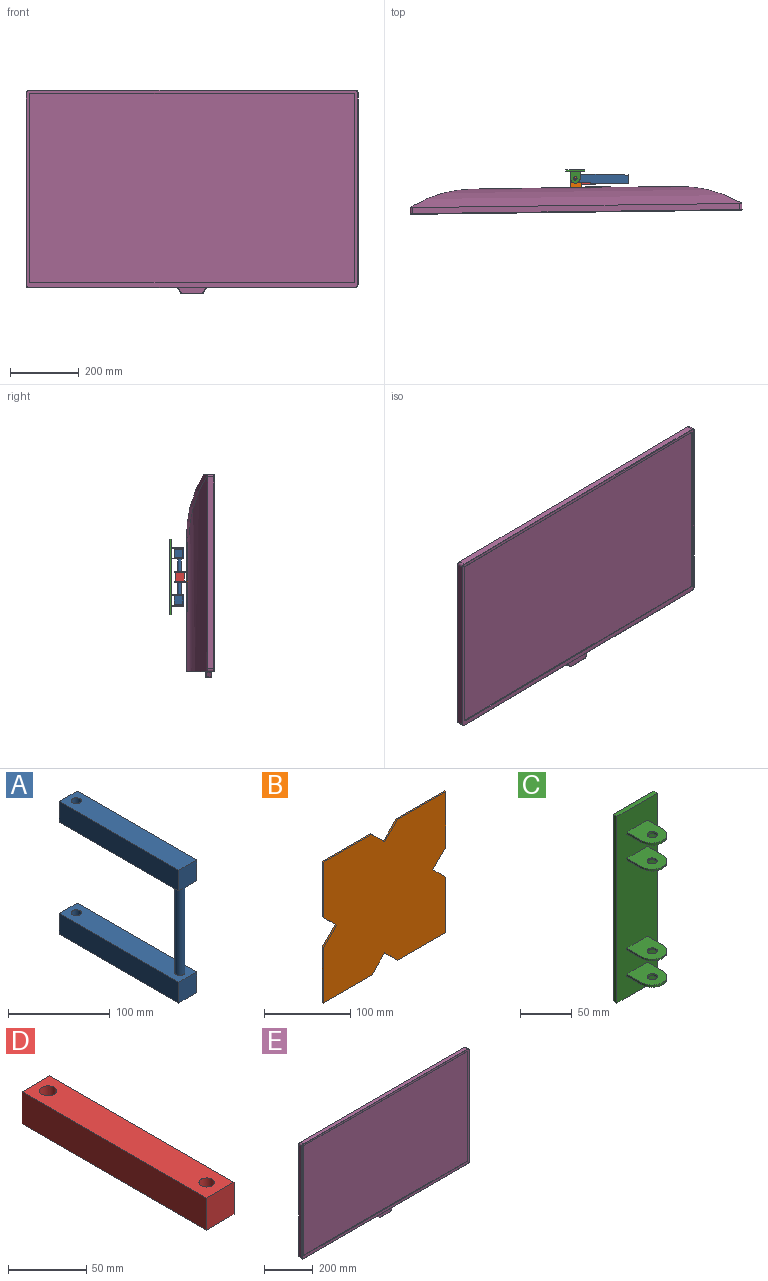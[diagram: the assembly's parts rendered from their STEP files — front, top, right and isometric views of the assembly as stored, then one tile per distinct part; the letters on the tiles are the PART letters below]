
ASSEMBLY  parts=5 mates=4
PART A: 15 faces, bbox 25x166x160 mm
  f0: plane 166x25mm, normal (-1,0,0), area 4150mm2, adj f1,f3,f5,f7
  f1: plane 25x25mm, normal (0,-1,0), area 625mm2, adj f0,f2,f5,f7
  f2: plane 166x25mm, normal (1,0,0), area 4150mm2, adj f1,f3,f5,f7
  f3: plane 25x25mm, normal (0,1,0), area 625mm2, adj f0,f2,f5,f7
  f4: cylinder r=5mm len=25mm, axis (0,0,-1), area 785.4mm2, adj f5,f7
  f5: plane 166x25mm, normal (0,0,1), area 4071.5mm2, adj f0,f1,f2,f3,f4
  f6: cylinder r=5mm len=110mm, axis (0,0,-1), area 3455.8mm2, adj f7,f8
  f7: plane 166x25mm, normal (0,0,-1), area 3992.9mm2, adj f0,f1,f2,f3,f4,f6
  f8: plane 166x25mm, normal (0,0,1), area 3992.9mm2, adj f6,f9,f10,f11,f12,f14
  f9: plane 25x25mm, normal (0,1,0), area 625mm2, adj f8,f10,f12,f13
  f10: plane 166x25mm, normal (1,0,0), area 4150mm2, adj f8,f9,f11,f13
  f11: plane 25x25mm, normal (0,-1,0), area 625mm2, adj f8,f10,f12,f13
  f12: plane 166x25mm, normal (-1,0,0), area 4150mm2, adj f8,f9,f11,f13
  f13: plane 166x25mm, normal (0,0,-1), area 4071.5mm2, adj f9,f10,f11,f12,f14
  f14: cylinder r=5mm len=25mm, axis (0,0,-1), area 785.4mm2, adj f8,f13
PART B: 30 faces, bbox 200x39x200 mm
  f0: plane 21x2.5mm, normal (-1,0,0), area 52.5mm2, adj f2,f4,f5,f6
  f1: plane 21x2.5mm, normal (1,0,0), area 52.5mm2, adj f2,f4,f5,f6
  f2: cylinder r=16mm len=32mm, axis (0,0,-1), area 125.7mm2, adj f0,f1,f4,f5
  f3: cylinder r=5mm len=10mm, axis (0,0,-1), area 78.5mm2, adj f4,f5
  f4: plane 37x32mm, normal (0,0,-1), area 995.6mm2, adj f0,f1,f2,f3,f6
  f5: plane 37x32mm, normal (0,0,1), area 995.6mm2, adj f0,f1,f2,f3,f6
  f6: plane 200x200mm, normal (0,1,0), area 38040mm2, adj f0,f1,f4,f5,f7,f8,f10,f12
  f7: plane 21x2.5mm, normal (1,0,0), area 52.5mm2, adj f6,f9,f10,f12
  f8: plane 21x2.5mm, normal (-1,0,0), area 52.5mm2, adj f6,f9,f10,f12
  f9: cylinder r=16mm len=32mm, axis (0,0,-1), area 125.7mm2, adj f7,f8,f10,f12
  f10: plane 37x32mm, normal (0,0,1), area 995.6mm2, adj f6,f7,f8,f9,f11
  f11: cylinder r=5mm len=10mm, axis (0,0,-1), area 78.5mm2, adj f10,f12
  f12: plane 37x32mm, normal (0,0,-1), area 995.6mm2, adj f6,f7,f8,f9,f11
  f13: plane 21.21x21.21mm, normal (0.71,0,0.71), area 60mm2, adj f6,f14,f28,f29
  f14: plane 78.79x2mm, normal (0,0,1), area 157.6mm2, adj f6,f13,f15,f29
  f15: plane 78.79x2mm, normal (-1,0,0), area 157.6mm2, adj f6,f14,f16,f29
  f16: plane 21.21x21.21mm, normal (-0.71,0,-0.71), area 60mm2, adj f6,f15,f17,f29
  f17: plane 21.21x21.21mm, normal (-0.71,0,0.71), area 60mm2, adj f6,f16,f18,f29
  f18: plane 78.79x2mm, normal (-1,0,0), area 157.6mm2, adj f6,f17,f19,f29
  f19: plane 78.79x2mm, normal (0,0,-1), area 157.6mm2, adj f6,f18,f20,f29
  f20: plane 21.21x21.21mm, normal (0.71,0,-0.71), area 60mm2, adj f6,f19,f21,f29
  f21: plane 21.21x21.21mm, normal (-0.71,0,-0.71), area 60mm2, adj f6,f20,f22,f29
  f22: plane 78.79x2mm, normal (0,0,-1), area 157.6mm2, adj f6,f21,f23,f29
  f23: plane 78.79x2mm, normal (1,0,0), area 157.6mm2, adj f6,f22,f24,f29
  f24: plane 21.21x21.21mm, normal (0.71,0,0.71), area 60mm2, adj f6,f23,f25,f29
  f25: plane 21.21x21.21mm, normal (0.71,0,-0.71), area 60mm2, adj f6,f24,f26,f29
  f26: plane 78.79x2mm, normal (1,0,0), area 157.6mm2, adj f6,f25,f27,f29
  f27: plane 78.79x2mm, normal (0,0,1), area 157.6mm2, adj f6,f26,f28,f29
  f28: plane 21.21x21.21mm, normal (-0.71,0,0.71), area 60mm2, adj f6,f13,f27,f29
  f29: plane 200x200mm, normal (0,-1,0), area 38200mm2, adj f13,f14,f15,f16,f17,f18,f19,f20
PART C: 30 faces, bbox 55x39.5x220 mm
  f0: plane 20.5x2mm, normal (1,0,0), area 41mm2, adj f3,f8,f27,f28
  f1: plane 20.5x2mm, normal (-1,0,0), area 41mm2, adj f3,f8,f27,f28
  f2: cylinder r=5mm len=10mm, axis (0,0,-1), area 62.8mm2, adj f27,f28
  f3: cylinder r=14mm len=28mm, axis (0,0,-1), area 88mm2, adj f0,f1,f27,f28
  f4: plane 20.5x2.5mm, normal (1,0,0), area 51.3mm2, adj f7,f8,f19,f20
  f5: plane 20.5x2.5mm, normal (-1,0,0), area 51.3mm2, adj f7,f8,f19,f20
  f6: cylinder r=5mm len=10mm, axis (0,0,-1), area 78.5mm2, adj f19,f20
  f7: cylinder r=14mm len=28mm, axis (0,0,-1), area 110mm2, adj f4,f5,f19,f20
  f8: plane 220x55mm, normal (0,-1,0), area 11848mm2, adj f0,f1,f4,f5,f9,f11,f12,f13
  f9: plane 220x5mm, normal (1,0,0), area 1100mm2, adj f8,f10,f12,f13
  f10: plane 220x55mm, normal (0,1,0), area 12100mm2, adj f9,f11,f12,f13
  f11: plane 220x5mm, normal (-1,0,0), area 1100mm2, adj f8,f10,f12,f13
  f12: plane 55x5mm, normal (0,0,1), area 275mm2, adj f8,f9,f10,f11
  f13: plane 55x5mm, normal (0,0,-1), area 275mm2, adj f8,f9,f10,f11
  f14: plane 20.5x2.5mm, normal (1,0,0), area 51.3mm2, adj f8,f17,f18,f21
  f15: plane 20.5x2.5mm, normal (-1,0,0), area 51.3mm2, adj f8,f17,f18,f21
  f16: cylinder r=5mm len=10mm, axis (0,0,-1), area 78.5mm2, adj f18,f21
  f17: cylinder r=14mm len=28mm, axis (0,0,-1), area 110mm2, adj f14,f15,f18,f21
  f18: plane 34.5x28mm, normal (0,0,1), area 803.3mm2, adj f8,f14,f15,f16,f17
  f19: plane 34.5x28mm, normal (0,0,-1), area 803.3mm2, adj f4,f5,f6,f7,f8
  f20: plane 34.5x28mm, normal (0,0,1), area 803.3mm2, adj f4,f5,f6,f7,f8
  f21: plane 34.5x28mm, normal (0,0,-1), area 803.3mm2, adj f8,f14,f15,f16,f17
  f22: plane 20.5x2mm, normal (1,0,0), area 41mm2, adj f8,f25,f26,f29
  f23: plane 20.5x2mm, normal (-1,0,0), area 41mm2, adj f8,f25,f26,f29
  f24: cylinder r=5mm len=10mm, axis (0,0,-1), area 62.8mm2, adj f26,f29
  f25: cylinder r=14mm len=28mm, axis (0,0,-1), area 88mm2, adj f22,f23,f26,f29
  f26: plane 34.5x28mm, normal (0,0,1), area 803.3mm2, adj f8,f22,f23,f24,f25
  f27: plane 34.5x28mm, normal (0,0,-1), area 803.3mm2, adj f0,f1,f2,f3,f8
  f28: plane 34.5x28mm, normal (0,0,1), area 803.3mm2, adj f0,f1,f2,f3,f8
  f29: plane 34.5x28mm, normal (0,0,-1), area 803.3mm2, adj f8,f22,f23,f24,f25
PART D: 8 faces, bbox 25x166x25 mm
  f0: plane 25x25mm, normal (0,1,0), area 625mm2, adj f1,f4,f5,f6
  f1: plane 166x25mm, normal (-1,0,0), area 4150mm2, adj f0,f2,f5,f6
  f2: plane 25x25mm, normal (0,-1,0), area 625mm2, adj f1,f4,f5,f6
  f3: cylinder r=5.5mm len=25mm, axis (0,0,-1), area 863.9mm2, adj f5,f6
  f4: plane 166x25mm, normal (1,0,0), area 4150mm2, adj f0,f2,f5,f6
  f5: plane 166x25mm, normal (0,0,1), area 3976.4mm2, adj f0,f1,f2,f3,f4,f7
  f6: plane 166x25mm, normal (0,0,-1), area 3976.4mm2, adj f0,f1,f2,f3,f4,f7
  f7: cylinder r=5mm len=25mm, axis (0,0,1), area 785.4mm2, adj f5,f6
PART E: 62 faces, bbox 968.3x70.6x594.1 mm
  f0: plane 951x17.6mm, normal (0,0,-1), area 15292.5mm2, adj f14,f15,f16,f19,f20,f26,f27,f33
  f1: plane 559.2x17.6mm, normal (1,0,0), area 9841.9mm2, adj f35,f38,f41,f47
  f2: plane 951x17.6mm, normal (0,0,1), area 16737.6mm2, adj f36,f38,f39,f48
  f3: plane 559.2x17.6mm, normal (-1,0,0), area 9841.9mm2, adj f37,f39,f40,f44
  f4: plane 599.87x390.64mm, normal (0,1,0), area 234330.6mm2, adj f34,f35,f36,f37
  f5: plane 547.2x0.6mm, normal (1,0,0), area 328.3mm2, adj f10,f52,f58,f61
  f6: plane 945x0.6mm, normal (0,0,-1), area 567mm2, adj f10,f55,f59,f61
  f7: plane 547.2x0.6mm, normal (-1,0,0), area 328.3mm2, adj f10,f50,f54,f55
  f8: plane 945x0.6mm, normal (0,0,1), area 567mm2, adj f10,f50,f52,f53
  f9: plane 965x573.2mm, normal (0,-1,0), area 30010.6mm2, adj f42,f43,f44,f45,f46,f47,f48,f49
  f10: plane 947x549.2mm, normal (0,-1,0), area 520091.5mm2, adj f5,f6,f7,f8,f50,f52,f55,f61
  f11: plane 12x11.69mm, normal (-0.87,0,-0.49), area 161.3mm2, adj f16,f17,f25,f32
  f12: plane 57.15x12mm, normal (0,0,-1), area 685.9mm2, adj f17,f18,f23,f30
  f13: plane 12x11.69mm, normal (0.87,0,-0.49), area 161.3mm2, adj f18,f19,f21,f28
  f14: plane 80.72x15.76mm, normal (0,1,0), area 1113.9mm2, adj f0,f20,f21,f22,f23,f24,f25,f26
  f15: plane 80.72x15.76mm, normal (0,-1,0), area 1113.9mm2, adj f0,f27,f28,f29,f30,f31,f32,f33
  f16: cylinder r=6mm len=12mm, axis (0,1,0), area 75.9mm2, adj f0,f11,f26,f33
  f17: cylinder r=6mm len=12mm, axis (0,-1,0), area 75.9mm2, adj f11,f12,f24,f31
  f18: cylinder r=6mm len=12mm, axis (0,-1,0), area 75.9mm2, adj f12,f13,f22,f29
  f19: cylinder r=6mm len=12mm, axis (0,1,0), area 75.9mm2, adj f0,f13,f20,f27
  f20: torus R=8mm, axis (0,-1,0), area 13.4mm2, adj f0,f14,f19,f21
  f21: cylinder r=2mm len=12.67mm, axis (-0.49,0,-0.87), area 42.2mm2, adj f13,f14,f20,f22
  f22: torus R=4mm, axis (0,-1,0), area 17.5mm2, adj f14,f18,f21,f23
  f23: cylinder r=2mm len=57.15mm, axis (-1,0,0), area 179.6mm2, adj f12,f14,f22,f24
  f24: torus R=4mm, axis (0,-1,0), area 17.5mm2, adj f14,f17,f23,f25
  f25: cylinder r=2mm len=12.67mm, axis (-0.49,0,0.87), area 42.2mm2, adj f11,f14,f24,f26
  f26: torus R=8mm, axis (0,-1,0), area 13.4mm2, adj f0,f14,f16,f25
  f27: torus R=8mm, axis (0,-1,0), area 13.4mm2, adj f0,f15,f19,f28
  f28: cylinder r=2mm len=12.67mm, axis (0.49,0,0.87), area 42.2mm2, adj f13,f15,f27,f29
  f29: torus R=4mm, axis (0,-1,0), area 17.5mm2, adj f15,f18,f28,f30
  f30: cylinder r=2mm len=57.15mm, axis (1,0,0), area 179.6mm2, adj f12,f15,f29,f31
  f31: torus R=4mm, axis (0,-1,0), area 17.5mm2, adj f15,f17,f30,f32
  f32: cylinder r=2mm len=12.67mm, axis (0.49,0,-0.87), area 42.2mm2, adj f11,f15,f31,f33
  f33: torus R=8mm, axis (0,-1,0), area 13.4mm2, adj f0,f15,f16,f32
  f34: plane 953.25x52mm, normal (0,0.02,-1), area 44098.8mm2, adj f0,f4,f35,f37,f40,f41
  f35: cylinder r=350mm len=572.78mm, axis (0,0,-1), area 93724.8mm2, adj f1,f4,f34,f36,f38,f41
  f36: cylinder r=350mm len=962.31mm, axis (1,0,0), area 152298.5mm2, adj f2,f4,f35,f37,f38,f39
  f37: cylinder r=350mm len=572.78mm, axis (0,0,1), area 93724.8mm2, adj f3,f4,f34,f36,f39,f40
  f38: cylinder r=8mm len=19.03mm, axis (0,1,0), area 227.3mm2, adj f1,f2,f35,f36,f49
  f39: cylinder r=8mm len=19.03mm, axis (0,-1,0), area 227.3mm2, adj f2,f3,f36,f37,f46
  f40: cylinder r=8mm len=21.73mm, axis (0,1,0), area 239.8mm2, adj f0,f3,f34,f37,f42
  f41: cylinder r=8mm len=21.73mm, axis (0,-1,0), area 239.8mm2, adj f0,f1,f34,f35,f45
  f42: torus R=7mm, axis (0,-1,0), area 18.8mm2, adj f9,f40,f43,f44
  f43: cylinder r=1mm len=951mm, axis (1,0,0), area 1493.8mm2, adj f0,f9,f42,f45
  f44: cylinder r=1mm len=559.2mm, axis (0,0,-1), area 878.4mm2, adj f3,f9,f42,f46
  f45: torus R=7mm, axis (0,-1,0), area 18.8mm2, adj f9,f41,f43,f47
  f46: torus R=7mm, axis (0,-1,0), area 18.8mm2, adj f9,f39,f44,f48
  f47: cylinder r=1mm len=559.2mm, axis (0,0,1), area 878.4mm2, adj f1,f9,f45,f49
  f48: cylinder r=1mm len=951mm, axis (-1,0,0), area 1493.8mm2, adj f2,f9,f46,f49
  f49: torus R=7mm, axis (0,-1,0), area 18.8mm2, adj f9,f38,f47,f48
  f50: cylinder r=1mm len=1mm, axis (0,1,0), area 0.9mm2, adj f7,f8,f10,f51
  f51: torus R=2mm, axis (0,-1,0), area 3.4mm2, adj f9,f50,f53,f54
  f52: cylinder r=1mm len=1mm, axis (0,-1,0), area 0.9mm2, adj f5,f8,f10,f56
  f53: cylinder r=1mm len=945mm, axis (1,0,0), area 1484.4mm2, adj f8,f9,f51,f56
  f54: cylinder r=1mm len=547.2mm, axis (0,0,1), area 859.5mm2, adj f7,f9,f51,f57
  f55: cylinder r=1mm len=1mm, axis (0,-1,0), area 0.9mm2, adj f6,f7,f10,f57
  f56: torus R=2mm, axis (0,-1,0), area 3.4mm2, adj f9,f52,f53,f58
  f57: torus R=2mm, axis (0,-1,0), area 3.4mm2, adj f9,f54,f55,f59
  f58: cylinder r=1mm len=547.2mm, axis (0,0,-1), area 859.5mm2, adj f5,f9,f56,f60
  f59: cylinder r=1mm len=945mm, axis (-1,0,0), area 1484.4mm2, adj f6,f9,f57,f60
  f60: torus R=2mm, axis (0,-1,0), area 3.4mm2, adj f9,f58,f59,f61
  f61: cylinder r=1mm len=1mm, axis (0,1,0), area 0.9mm2, adj f5,f6,f10,f60
PLACE A rot(axis=(0,0,1),89deg) t=(115.42,129.88,17.14)mm
PLACE B rot(axis=(0,0,1),0.7deg) t=(-40.24,260.25,17.14)mm
PLACE C t=(-39.56,-22.41,17.14)mm fixed
PLACE D rot(axis=(0,0,-1),89.3deg) t=(93.42,129.94,17.14)mm
PLACE E rot(axis=(0,0,1),0.7deg) t=(-520.86,30.15,-259.18)mm
MATE revolute B.f2 <-> D.f7  axis (0,0,1) through (-38.57,128.26,3.64)mm
MATE revolute D.f3 <-> A.f6  axis (0,0,-1) through (104.42,130.08,17.14)mm
MATE revolute A.f4 <-> C.f2  axis (0,0,1) through (-39.56,132.59,97.14)mm
MATE fastened E.f4 <-> B.f29  axis (-0.01,1,0) through (-38.27,105.27,-62.86)mm
